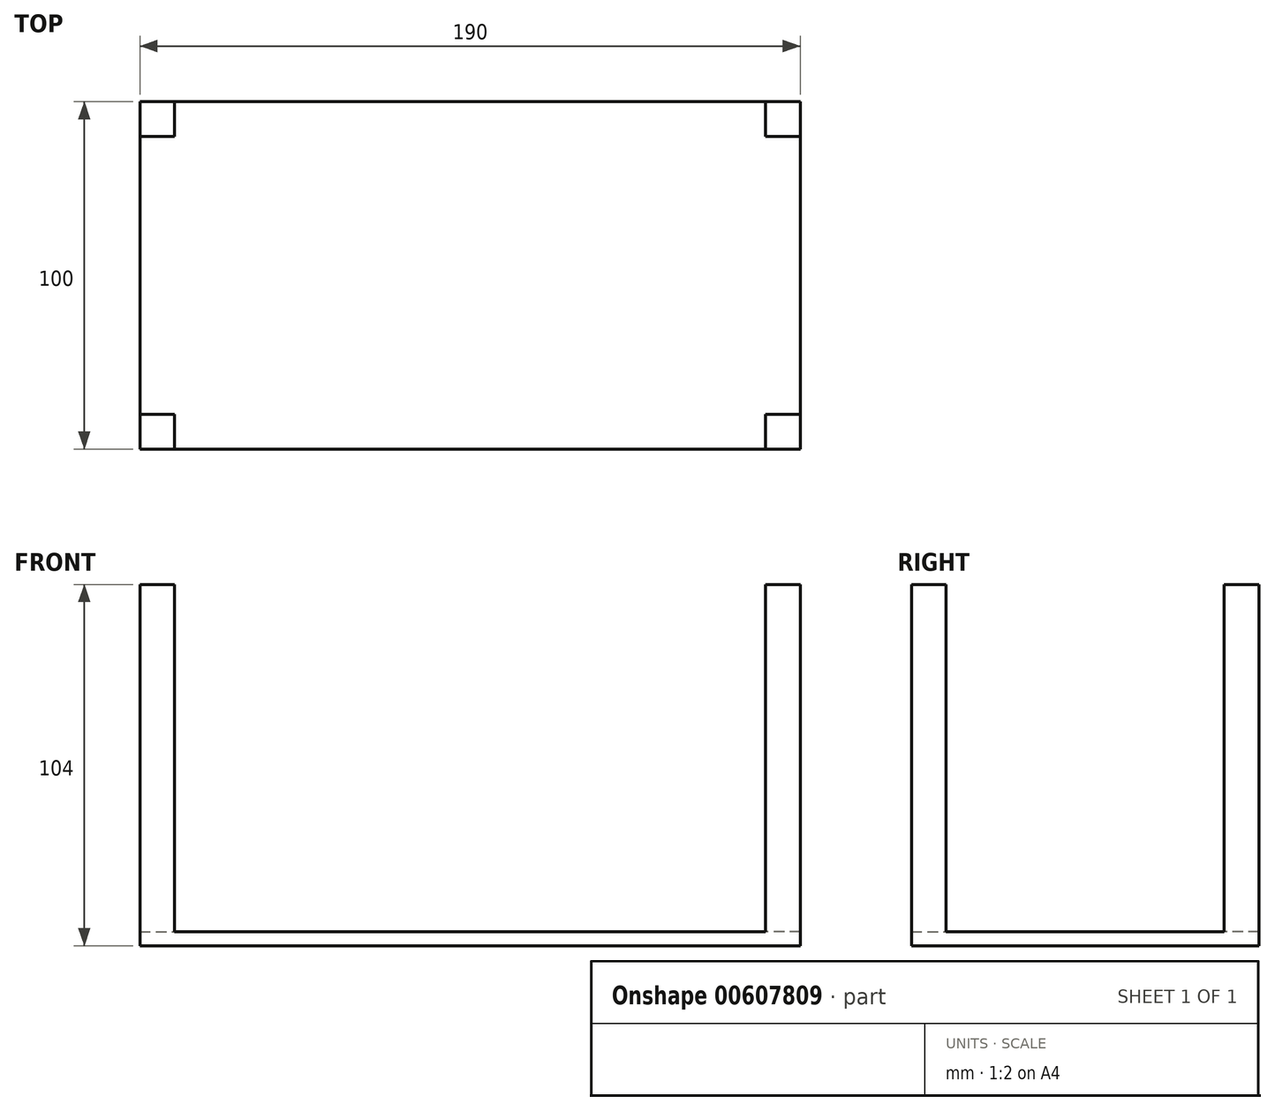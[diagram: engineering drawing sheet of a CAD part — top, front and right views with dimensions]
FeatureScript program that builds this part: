
annotation { "Feature Type Name" : "Feature", "Feature Type Description" : "" }
export const myFeature = defineFeature(function(context is Context, id is Id, definition is map)
    precondition{}
    {
        {
            var Q0;
            Q0=qCreatedBy(makeId("Top.planeOp"),FACE);
            var sketch = newSketch(context, id + "F0", { "sketchPlane" : qUnion([Q0])});
            skLineSegment(sketch, "E0.bottom", {"start": v(-97.9, 53.27) * mm, "end": v(92.1, 53.27) * mm});
            skLineSegment(sketch, "E0.top", {"start": v(-97.9, -46.73) * mm, "end": v(92.1, -46.73) * mm});
            skLineSegment(sketch, "E0.left", {"start": v(-97.9, 53.27) * mm, "end": v(-97.9, -46.73) * mm});
            skLineSegment(sketch, "E0.right", {"start": v(92.1, 53.27) * mm, "end": v(92.1, -46.73) * mm});
            skSolve(sketch);
        }
        {
            var Q0;
            Q0=makeQuery(id+"F0.imprint","IMPRINT",FACE,{"disambiguationData":[TD([[makeQuery(id+"F0.imprint","IMPRINT",EDGE,{"derivedFrom":sQuery(id+"F0.wireOp",EDGE,"E0.bottom")}),-1.0]])]});
            extrude(context, id + "F1", {"entities" : qUnion([Q0]), "depth" : 4 * mm, "offsetDistance" : 25 * mm});
        }
        {
            var Q0;
            Q0=makeQuery(id+"F1.opExtrude","CAP_FACE",FACE,{"disambiguationData":[OSD([sQuery(id+"F0.wireOp",EDGE,"E0.bottom"),sQuery(id+"F0.wireOp",EDGE,"E0.top"),sQuery(id+"F0.wireOp",EDGE,"E0.left"),sQuery(id+"F0.wireOp",EDGE,"E0.right")])],"isStart":false});
            var sketch = newSketch(context, id + "F2", { "sketchPlane" : qUnion([Q0])});
            skLineSegment(sketch, "E1.bottom", {"start": v(-97.9, -46.73) * mm, "end": v(-87.9, -46.73) * mm});
            skLineSegment(sketch, "E1.top", {"start": v(-97.9, -36.73) * mm, "end": v(-87.9, -36.73) * mm});
            skLineSegment(sketch, "E1.left", {"start": v(-97.9, -46.73) * mm, "end": v(-97.9, -36.73) * mm});
            skLineSegment(sketch, "E1.right", {"start": v(-87.9, -46.73) * mm, "end": v(-87.9, -36.73) * mm});
            skPoint(sketch, "E2.oppositeSnap0", {"position": v(-87.9, -41.73) * mm});
            skLineSegment(sketch, "E2.bottom", {"start": v(-97.9, 53.27) * mm, "end": v(-87.9, 53.27) * mm});
            skLineSegment(sketch, "E2.top", {"start": v(-97.9, 43.27) * mm, "end": v(-87.9, 43.27) * mm});
            skLineSegment(sketch, "E2.left", {"start": v(-97.9, 53.27) * mm, "end": v(-97.9, 43.27) * mm});
            skLineSegment(sketch, "E2.right", {"start": v(-87.9, 53.27) * mm, "end": v(-87.9, 43.27) * mm});
            skLineSegment(sketch, "E3.bottom", {"start": v(92.1, 53.27) * mm, "end": v(82.1, 53.27) * mm});
            skLineSegment(sketch, "E3.top", {"start": v(92.1, 43.27) * mm, "end": v(82.1, 43.27) * mm});
            skLineSegment(sketch, "E3.left", {"start": v(92.1, 53.27) * mm, "end": v(92.1, 43.27) * mm});
            skLineSegment(sketch, "E3.right", {"start": v(82.1, 53.27) * mm, "end": v(82.1, 43.27) * mm});
            skLineSegment(sketch, "E4.bottom", {"start": v(92.1, -46.73) * mm, "end": v(82.1, -46.73) * mm});
            skLineSegment(sketch, "E4.top", {"start": v(92.1, -36.73) * mm, "end": v(82.1, -36.73) * mm});
            skLineSegment(sketch, "E4.left", {"start": v(92.1, -46.73) * mm, "end": v(92.1, -36.73) * mm});
            skLineSegment(sketch, "E4.right", {"start": v(82.1, -46.73) * mm, "end": v(82.1, -36.73) * mm});
            skSolve(sketch);
        }
        {
            var Q0;
            Q0 = qSketchRegion(id + "F2", true);
            extrude(context, id + "F3", {"entities" : qUnion([Q0]), "operationType" : NewBodyOperationType.ADD, "depth" : 100 * mm, "offsetDistance" : 25 * mm});
        }
    });
